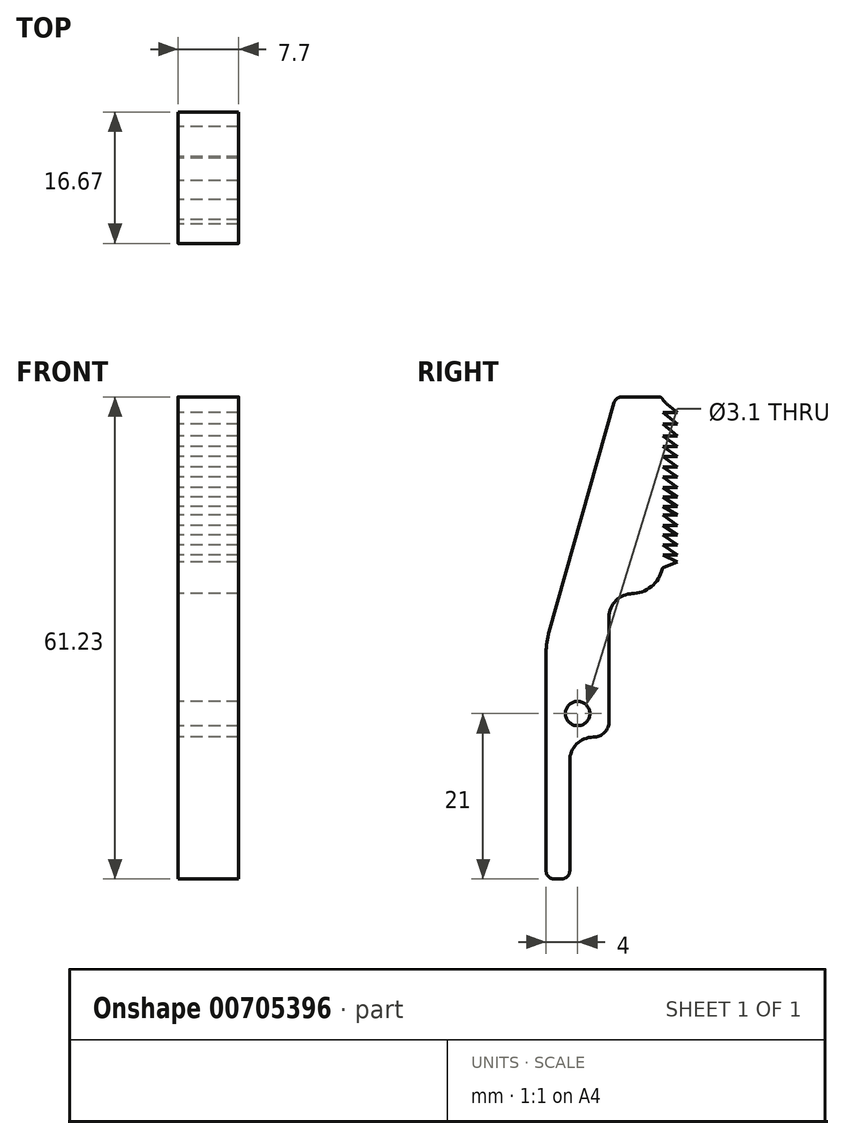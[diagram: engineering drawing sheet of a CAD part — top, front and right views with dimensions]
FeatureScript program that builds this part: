
annotation { "Feature Type Name" : "Feature", "Feature Type Description" : "" }
export const myFeature = defineFeature(function(context is Context, id is Id, definition is map)
    precondition{}
    {
        {
            var Q0;
            Q0=qCreatedBy(makeId("Right.planeOp"),FACE);
            var sketch = newSketch(context, id + "F0", { "sketchPlane" : qUnion([Q0])});
            skLineSegment(sketch, "E0", {"start": v(0, 1) * mm, "end": v(0, 28.61) * mm});
            skLineSegment(sketch, "E1", {"start": v(0, 30) * mm, "end": v(8, 30) * mm});
            skLineSegment(sketch, "E2", {"start": v(8, 30) * mm, "end": v(8, 20) * mm});
            skLineSegment(sketch, "E3", {"start": v(6, 18) * mm, "end": v(6, 18) * mm});
            skLineSegment(sketch, "E4", {"start": v(3, 15) * mm, "end": v(3, 1) * mm});
            skLineSegment(sketch, "E5", {"start": v(2, 0) * mm, "end": v(1, 0) * mm});
            skCircle(sketch, "E6", {"center": v(4, 21) * mm, "radius": 1.55 * mm});
            skLineSegment(sketch, "E7", {"start": v(11, 36.23) * mm, "end": v(10.84, 36.23) * mm});
            skLineSegment(sketch, "E8", {"start": v(8, 33.23) * mm, "end": v(8, 30) * mm});
            skLineSegment(sketch, "E9", {"start": v(14.84, 40.23) * mm, "end": v(14.84, 60.73) * mm});
            skLineSegment(sketch, "E10", {"start": v(14.34, 61.23) * mm, "end": v(9.6, 61.23) * mm});
            skLineSegment(sketch, "E11", {"start": v(8.64, 60.5) * mm, "end": v(0.38, 31.34) * mm});
            skPoint(sketch, "E12.visualSharp", {"position": v(8, 18) * mm});
            skArc(sketch, "E12.filletArc", {"start": v(6, 18) * mm, "mid": v(7.41, 18.59) * mm, "end": v(8, 20) * mm});
            skPoint(sketch, "E13.visualSharp", {"position": v(3, 18) * mm});
            skArc(sketch, "E13.filletArc", {"start": v(6, 18) * mm, "mid": v(3.88, 17.12) * mm, "end": v(3, 15) * mm});
            skPoint(sketch, "E14.visualSharp", {"position": v(8, 36.23) * mm});
            skArc(sketch, "E14.filletArc", {"start": v(11, 36.23) * mm, "mid": v(8.88, 35.35) * mm, "end": v(8, 33.23) * mm});
            skPoint(sketch, "E15.visualSharp", {"position": v(14.84, 36.23) * mm});
            skArc(sketch, "E15.filletArc", {"start": v(10.84, 36.23) * mm, "mid": v(13.36, 37.12) * mm, "end": v(14.76, 39.4) * mm});
            skPoint(sketch, "E16.visualSharp", {"position": v(8.84, 61.23) * mm});
            skArc(sketch, "E16.filletArc", {"start": v(9.6, 61.23) * mm, "mid": v(9, 61.02) * mm, "end": v(8.64, 60.5) * mm});
            skPoint(sketch, "E17.visualSharp", {"position": v(0, 30) * mm});
            skArc(sketch, "E17.filletArc", {"start": v(0.38, 31.34) * mm, "mid": v(0.1, 29.99) * mm, "end": v(0, 28.61) * mm});
            skPoint(sketch, "E18.visualSharp", {"position": v(0, 0) * mm});
            skArc(sketch, "E18.filletArc", {"start": v(0, 1) * mm, "mid": v(0.3, 0.3) * mm, "end": v(1, 0) * mm});
            skPoint(sketch, "E19.visualSharp", {"position": v(3, 0) * mm});
            skArc(sketch, "E19.filletArc", {"start": v(2, 0) * mm, "mid": v(2.7, 0.3) * mm, "end": v(3, 1) * mm});
            skPoint(sketch, "E20.visualSharp", {"position": v(14.84, 61.23) * mm});
            skArc(sketch, "E20.filletArc", {"start": v(14.76, 61) * mm, "mid": v(14.58, 61.16) * mm, "end": v(14.34, 61.23) * mm});
            skLineSegment(sketch, "E21", {"start": v(15.41, 60.26) * mm, "end": v(16.67, 59.24) * mm});
            skLineSegment(sketch, "E22", {"start": v(16.67, 59.24) * mm, "end": v(14.84, 59.24) * mm});
            skLineSegment(sketch, "E23", {"start": v(14.84, 59.24) * mm, "end": v(16.67, 57.75) * mm});
            skLineSegment(sketch, "E24", {"start": v(16.67, 57.75) * mm, "end": v(14.84, 57.75) * mm});
            skLineSegment(sketch, "E25", {"start": v(14.84, 57.75) * mm, "end": v(16.67, 56.27) * mm});
            skLineSegment(sketch, "E26", {"start": v(16.67, 56.27) * mm, "end": v(14.84, 56.27) * mm});
            skLineSegment(sketch, "E27", {"start": v(14.84, 56.27) * mm, "end": v(16.67, 54.95) * mm});
            skLineSegment(sketch, "E28", {"start": v(16.67, 54.95) * mm, "end": v(14.84, 54.95) * mm});
            skLineSegment(sketch, "E29", {"start": v(14.84, 54.95) * mm, "end": v(16.67, 53.68) * mm});
            skLineSegment(sketch, "E30", {"start": v(16.67, 53.68) * mm, "end": v(14.84, 53.68) * mm});
            skLineSegment(sketch, "E31", {"start": v(14.84, 53.68) * mm, "end": v(16.67, 52.3) * mm});
            skLineSegment(sketch, "E32", {"start": v(16.67, 52.3) * mm, "end": v(14.84, 52.3) * mm});
            skLineSegment(sketch, "E33", {"start": v(14.84, 52.3) * mm, "end": v(16.67, 51.02) * mm});
            skLineSegment(sketch, "E34", {"start": v(16.67, 51.02) * mm, "end": v(14.84, 51.02) * mm});
            skLineSegment(sketch, "E35", {"start": v(14.84, 51.02) * mm, "end": v(16.67, 49.74) * mm});
            skLineSegment(sketch, "E36", {"start": v(16.67, 49.74) * mm, "end": v(14.84, 49.74) * mm});
            skLineSegment(sketch, "E37", {"start": v(14.84, 49.74) * mm, "end": v(16.67, 48.53) * mm});
            skLineSegment(sketch, "E38", {"start": v(16.67, 48.53) * mm, "end": v(14.84, 48.53) * mm});
            skLineSegment(sketch, "E39", {"start": v(14.84, 48.53) * mm, "end": v(16.67, 47.3) * mm});
            skLineSegment(sketch, "E40", {"start": v(16.67, 47.3) * mm, "end": v(14.84, 47.3) * mm});
            skLineSegment(sketch, "E41", {"start": v(14.84, 47.3) * mm, "end": v(16.67, 46.2) * mm});
            skLineSegment(sketch, "E42", {"start": v(16.67, 46.2) * mm, "end": v(14.84, 46.2) * mm});
            skLineSegment(sketch, "E43", {"start": v(14.84, 46.2) * mm, "end": v(16.67, 44.92) * mm});
            skLineSegment(sketch, "E44", {"start": v(16.67, 44.92) * mm, "end": v(14.84, 44.92) * mm});
            skLineSegment(sketch, "E45", {"start": v(14.84, 44.92) * mm, "end": v(16.67, 43.68) * mm});
            skLineSegment(sketch, "E46", {"start": v(16.67, 43.68) * mm, "end": v(14.84, 43.68) * mm});
            skLineSegment(sketch, "E47", {"start": v(14.84, 43.68) * mm, "end": v(16.67, 42.4) * mm});
            skLineSegment(sketch, "E48", {"start": v(16.67, 42.4) * mm, "end": v(14.84, 42.4) * mm});
            skLineSegment(sketch, "E49", {"start": v(14.84, 42.4) * mm, "end": v(16.67, 41.12) * mm});
            skLineSegment(sketch, "E50", {"start": v(16.67, 41.12) * mm, "end": v(14.84, 41.12) * mm});
            skLineSegment(sketch, "E51", {"start": v(14.84, 41.12) * mm, "end": v(16.67, 40.23) * mm});
            skPoint(sketch, "E52.visualSharp", {"position": v(14.84, 40.23) * mm});
            skArc(sketch, "E52.filletArc", {"start": v(15.03, 40.23) * mm, "mid": v(14.9, 40.17) * mm, "end": v(14.84, 40.04) * mm});
            skLineSegment(sketch, "E53", {"start": v(14.84, 60.73) * mm, "end": v(14.84, 41.12) * mm});
            skLineSegment(sketch, "E54", {"start": v(16.67, 40.23) * mm, "end": v(14.88, 39.55) * mm});
            skArc(sketch, "E55.filletArc", {"start": v(14.88, 39.55) * mm, "mid": v(14.8, 39.5) * mm, "end": v(14.76, 39.4) * mm});
            skPoint(sketch, "E56.visualSharp", {"position": v(14.84, 60.73) * mm});
            skArc(sketch, "E56.filletArc", {"start": v(14.76, 61) * mm, "mid": v(15.06, 60.6) * mm, "end": v(15.41, 60.26) * mm});
            skSolve(sketch);
        }
        {
            var Q0;
            Q0=makeQuery(id+"F0.imprint","IMPRINT",FACE,{"disambiguationData":[TD([[makeQuery(id+"F0.imprint","IMPRINT",EDGE,{"derivedFrom":sQuery(id+"F0.wireOp",EDGE,"E7")}),1.0]])]});
            var Q1;
            {var subQ1=sQuery(id+"F0.wireOp",EDGE,"E0");Q1=makeQuery(id+"F0.imprint","IMPRINT",FACE,{"disambiguationData":[TD([[makeQuery(id+"F0.imprint","IMPRINT",EDGE,{"derivedFrom":subQ1}),-1.0]])]});}
            var Q2;
            {var subQ0=sQuery(id+"F0.wireOp",EDGE,"E21");Q2=makeQuery(id+"F0.imprint","IMPRINT",FACE,{"disambiguationData":[TD([[makeQuery(id+"F0.imprint","IMPRINT",EDGE,{"derivedFrom":subQ0}),-1.0]])]});}
            var Q3;
            {var subQ0=sQuery(id+"F0.wireOp",EDGE,"E49");Q3=makeQuery(id+"F0.imprint","IMPRINT",FACE,{"disambiguationData":[TD([[makeQuery(id+"F0.imprint","IMPRINT",EDGE,{"derivedFrom":subQ0}),-1.0]])]});}
            var Q4;
            {var subQ0=sQuery(id+"F0.wireOp",EDGE,"E47");Q4=makeQuery(id+"F0.imprint","IMPRINT",FACE,{"disambiguationData":[TD([[makeQuery(id+"F0.imprint","IMPRINT",EDGE,{"derivedFrom":subQ0}),-1.0]])]});}
            var Q5;
            {var subQ0=sQuery(id+"F0.wireOp",EDGE,"E45");Q5=makeQuery(id+"F0.imprint","IMPRINT",FACE,{"disambiguationData":[TD([[makeQuery(id+"F0.imprint","IMPRINT",EDGE,{"derivedFrom":subQ0}),-1.0]])]});}
            var Q6;
            {var subQ0=sQuery(id+"F0.wireOp",EDGE,"E43");Q6=makeQuery(id+"F0.imprint","IMPRINT",FACE,{"disambiguationData":[TD([[makeQuery(id+"F0.imprint","IMPRINT",EDGE,{"derivedFrom":subQ0}),-1.0]])]});}
            var Q7;
            {var subQ0=sQuery(id+"F0.wireOp",EDGE,"E41");Q7=makeQuery(id+"F0.imprint","IMPRINT",FACE,{"disambiguationData":[TD([[makeQuery(id+"F0.imprint","IMPRINT",EDGE,{"derivedFrom":subQ0}),-1.0]])]});}
            var Q8;
            {var subQ0=sQuery(id+"F0.wireOp",EDGE,"E35");Q8=makeQuery(id+"F0.imprint","IMPRINT",FACE,{"disambiguationData":[TD([[makeQuery(id+"F0.imprint","IMPRINT",EDGE,{"derivedFrom":subQ0}),-1.0]])]});}
            var Q9;
            {var subQ0=sQuery(id+"F0.wireOp",EDGE,"E39");Q9=makeQuery(id+"F0.imprint","IMPRINT",FACE,{"disambiguationData":[TD([[makeQuery(id+"F0.imprint","IMPRINT",EDGE,{"derivedFrom":subQ0}),-1.0]])]});}
            var Q10;
            {var subQ0=sQuery(id+"F0.wireOp",EDGE,"E37");Q10=makeQuery(id+"F0.imprint","IMPRINT",FACE,{"disambiguationData":[TD([[makeQuery(id+"F0.imprint","IMPRINT",EDGE,{"derivedFrom":subQ0}),-1.0]])]});}
            var Q11;
            {var subQ0=sQuery(id+"F0.wireOp",EDGE,"E33");Q11=makeQuery(id+"F0.imprint","IMPRINT",FACE,{"disambiguationData":[TD([[makeQuery(id+"F0.imprint","IMPRINT",EDGE,{"derivedFrom":subQ0}),-1.0]])]});}
            var Q12;
            {var subQ0=sQuery(id+"F0.wireOp",EDGE,"E31");Q12=makeQuery(id+"F0.imprint","IMPRINT",FACE,{"disambiguationData":[TD([[makeQuery(id+"F0.imprint","IMPRINT",EDGE,{"derivedFrom":subQ0}),-1.0]])]});}
            var Q13;
            {var subQ0=sQuery(id+"F0.wireOp",EDGE,"E29");Q13=makeQuery(id+"F0.imprint","IMPRINT",FACE,{"disambiguationData":[TD([[makeQuery(id+"F0.imprint","IMPRINT",EDGE,{"derivedFrom":subQ0}),-1.0]])]});}
            var Q14;
            {var subQ0=sQuery(id+"F0.wireOp",EDGE,"E27");Q14=makeQuery(id+"F0.imprint","IMPRINT",FACE,{"disambiguationData":[TD([[makeQuery(id+"F0.imprint","IMPRINT",EDGE,{"derivedFrom":subQ0}),-1.0]])]});}
            var Q15;
            {var subQ0=sQuery(id+"F0.wireOp",EDGE,"E25");Q15=makeQuery(id+"F0.imprint","IMPRINT",FACE,{"disambiguationData":[TD([[makeQuery(id+"F0.imprint","IMPRINT",EDGE,{"derivedFrom":subQ0}),-1.0]])]});}
            var Q16;
            {var subQ0=sQuery(id+"F0.wireOp",EDGE,"E23");Q16=makeQuery(id+"F0.imprint","IMPRINT",FACE,{"disambiguationData":[TD([[makeQuery(id+"F0.imprint","IMPRINT",EDGE,{"derivedFrom":subQ0}),-1.0]])]});}
            extrude(context, id + "F1", {"entities" : qUnion([Q0, Q1, Q2, Q3, Q4, Q5, Q6, Q7, Q8, Q9, Q10, Q11, Q12, Q13, Q14, Q15, Q16]), "depth" : 7.7 * mm, "offsetDistance" : 25 * mm});
        }
    });
